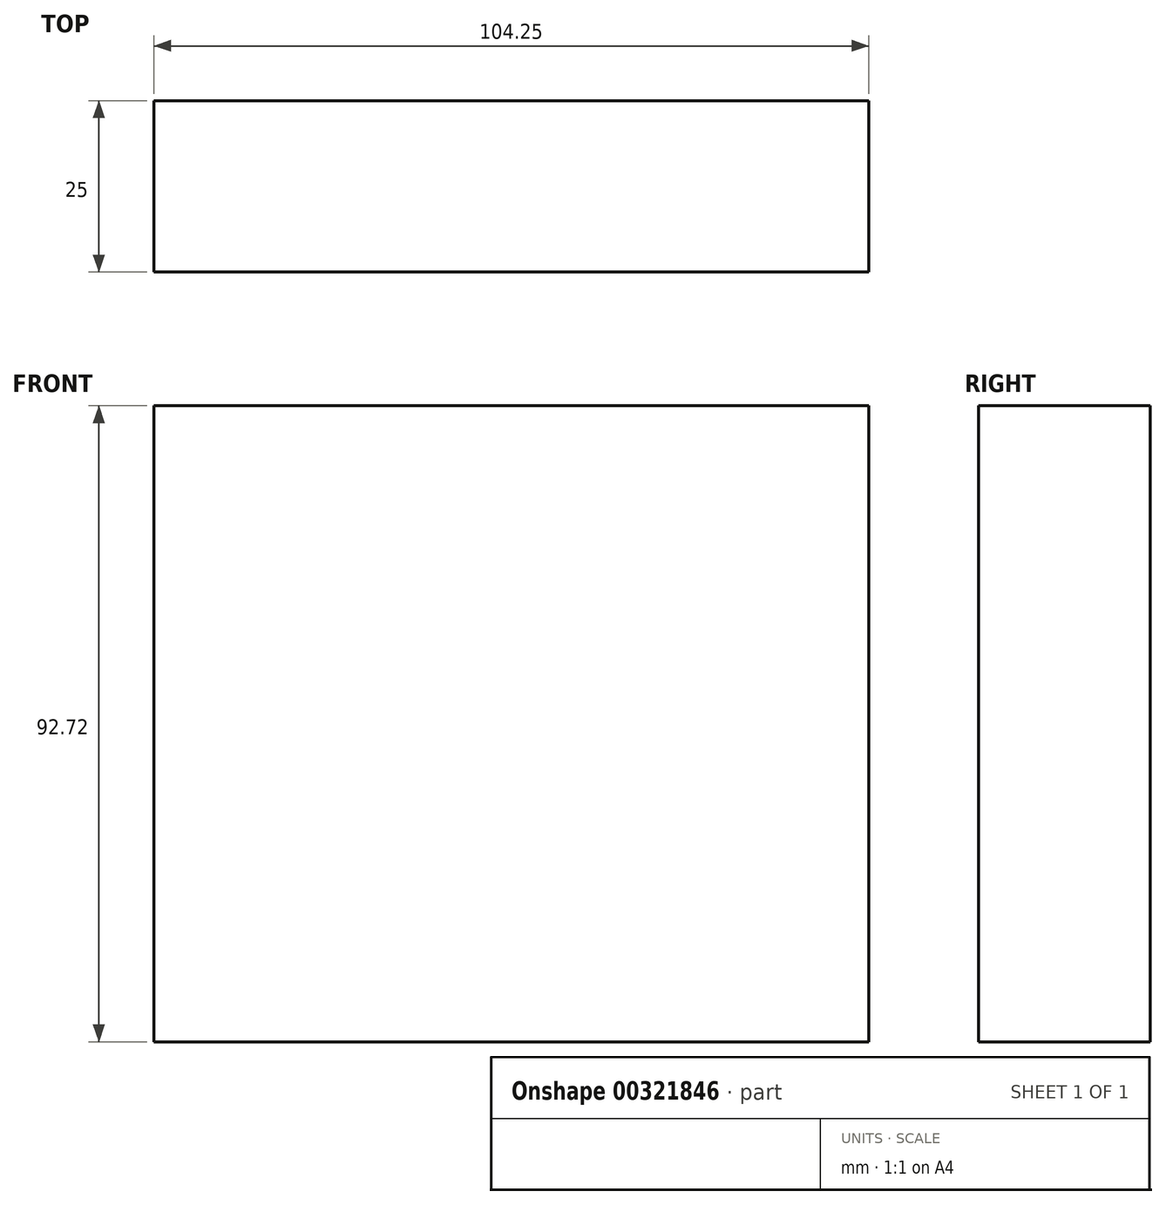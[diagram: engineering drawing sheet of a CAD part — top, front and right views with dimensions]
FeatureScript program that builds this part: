
annotation { "Feature Type Name" : "Feature", "Feature Type Description" : "" }
export const myFeature = defineFeature(function(context is Context, id is Id, definition is map)
    precondition{}
    {
        {
            var Q0;
            Q0=qCreatedBy(makeId("Front.planeOp"),FACE);
            var sketch = newSketch(context, id + "F0", { "sketchPlane" : qUnion([Q0])});
            skLineSegment(sketch, "E0.bottom", {"start": v(-60.32, 65.54) * mm, "end": v(43.93, 65.54) * mm});
            skLineSegment(sketch, "E0.top", {"start": v(-60.32, -27.18) * mm, "end": v(43.93, -27.18) * mm});
            skLineSegment(sketch, "E0.left", {"start": v(-60.32, 65.54) * mm, "end": v(-60.32, -27.18) * mm});
            skLineSegment(sketch, "E0.right", {"start": v(43.93, 65.54) * mm, "end": v(43.93, -27.18) * mm});
            skSolve(sketch);
        }
        {
            var Q0;
            Q0 = qSketchRegion(id + "F0", true);
            extrude(context, id + "F1", {"entities" : qUnion([Q0]), "depth" : 25 * mm});
        }
    });
